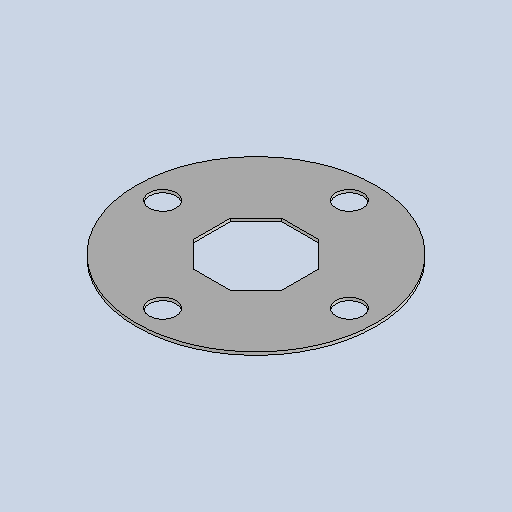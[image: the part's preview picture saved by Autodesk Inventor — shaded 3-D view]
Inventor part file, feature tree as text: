
AUTODESK INVENTOR PART (.ipt)
format: ipt  version: 2025.3 (Build 293356030, 356C)  size: 219,136 bytes
history: native  units: mm
features: sketch x2, other x2, sheet_metal_op x1
ambient origin geometry x8: Origin, YZ Plane, XZ Plane, XY Plane, X Axis, Y Axis, Z Axis, Center Point
bodies: Body1 (feature_tree)
feature tree (5):
  sheet_metal_op  "Face3"
  sketch  "Sketch1"  dims[d156=2.0mm]
  other  "Plate5"
  sketch  "Sketch Circular Pattern1"  dims[d177=360.0deg]
  other  "Definition1"
